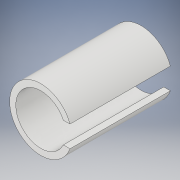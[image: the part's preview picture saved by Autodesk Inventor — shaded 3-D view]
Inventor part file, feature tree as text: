
AUTODESK INVENTOR PART (.ipt)
format: ipt  version: 2017 (Build 210142000, 142)  size: 109,056 bytes
history: native  units: in
note: dims shown in document units (in); Inventor stores cm internally (conversion verified against a paired STEP export)
features: extrude x2, sketch x2
ambient origin geometry x8: Origin, YZ Plane, XZ Plane, XY Plane, X Axis, Y Axis, Z Axis, Center Point
bodies: Solid1 (feature_tree)
feature tree (4):
  extrude  "Extrusion1"  Depth=1.0551in
  extrude  "Extrusion4"  Depth=0.4528in
  sketch  "Sketch1"  dims[d0=1.316in d1=1.0551in]
  sketch  "Sketch4"  dims[d2=2.122in d3=0.0in d9=0.7874in d10=0.4528in d11=0.0in d12=0.0in]
